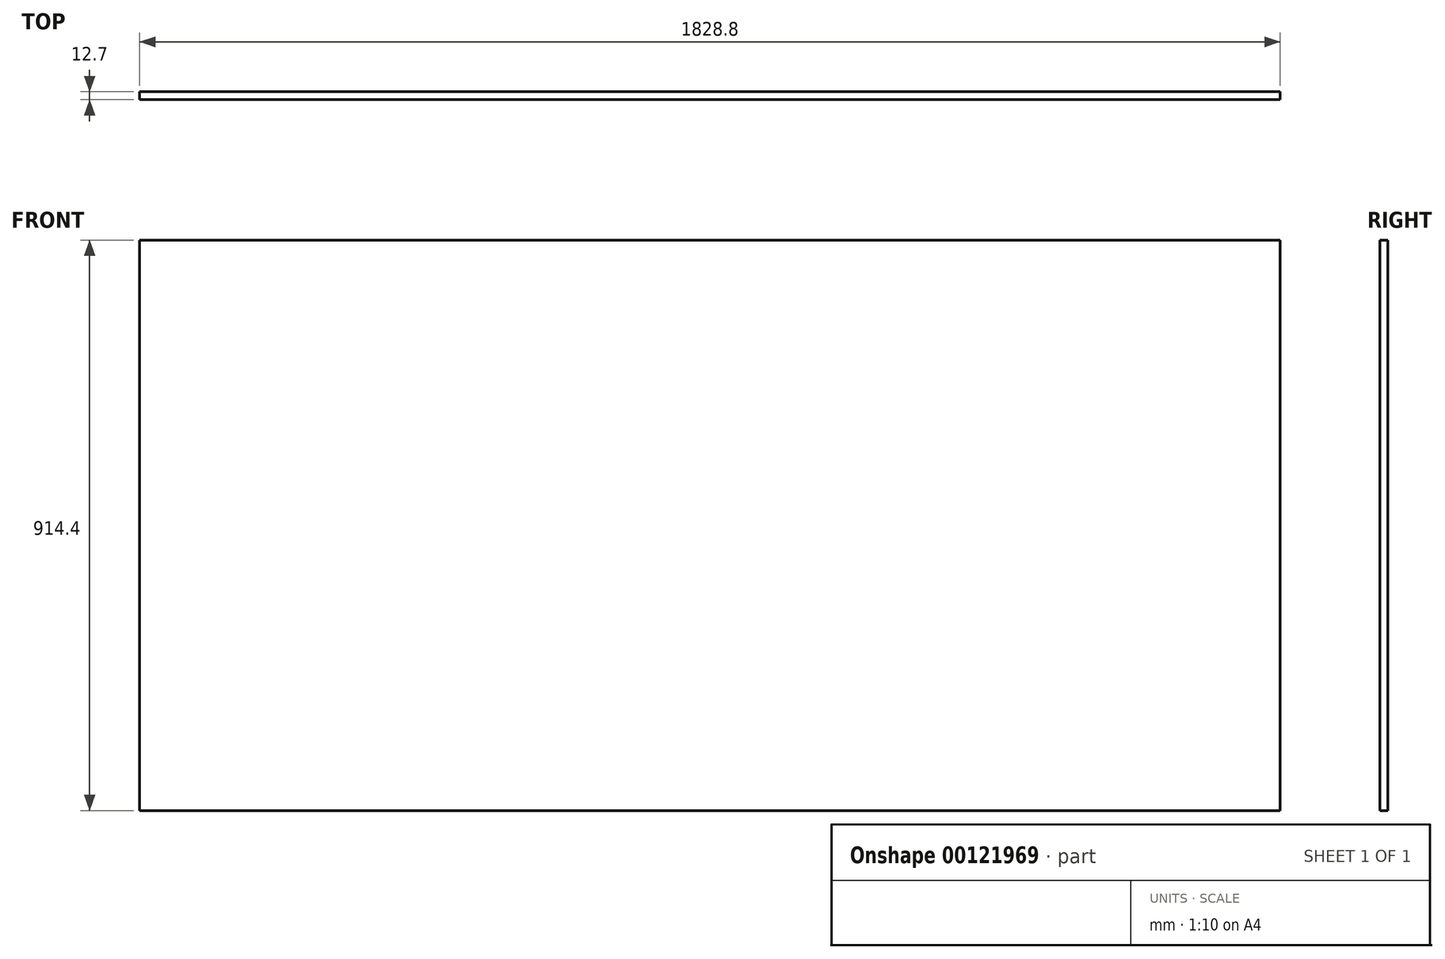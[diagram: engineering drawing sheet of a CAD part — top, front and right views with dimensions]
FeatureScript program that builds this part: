
annotation { "Feature Type Name" : "Feature", "Feature Type Description" : "" }
export const myFeature = defineFeature(function(context is Context, id is Id, definition is map)
    precondition{}
    {
        {
            var Q0;
            Q0=qCreatedBy(makeId("Front.planeOp"),FACE);
            var sketch = newSketch(context, id + "F0", { "sketchPlane" : qUnion([Q0])});
            skLineSegment(sketch, "E0.bottom", {"start": v(0, 0) * mm, "end": v(1828.8, 0) * mm});
            skLineSegment(sketch, "E0.top", {"start": v(0, 914.4) * mm, "end": v(1828.8, 914.4) * mm});
            skLineSegment(sketch, "E0.left", {"start": v(0, 0) * mm, "end": v(0, 914.4) * mm});
            skLineSegment(sketch, "E0.right", {"start": v(1828.8, 0) * mm, "end": v(1828.8, 914.4) * mm});
            skSolve(sketch);
        }
        {
            var Q0;
            Q0=makeQuery(id+"F0.imprint","IMPRINT",FACE,{"disambiguationData":[TD([[makeQuery(id+"F0.imprint","IMPRINT",EDGE,{"derivedFrom":sQuery(id+"F0.wireOp",EDGE,"E0.bottom")}),1.0]])]});
            extrude(context, id + "F1", {"entities" : qUnion([Q0]), "depth" : 12.7 * mm});
        }
    });
